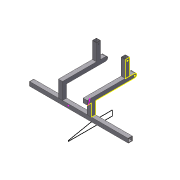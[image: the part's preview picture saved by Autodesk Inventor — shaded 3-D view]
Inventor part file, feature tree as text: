
AUTODESK INVENTOR PART (.ipt)
format: ipt  version: 2012 (Build 160160000, 160)  size: 230,912 bytes
history: native  units: in
note: dims shown in document units (in); Inventor stores cm internally (conversion verified against a paired STEP export)
features: sketch x8, extrude x7, shell x2, pattern_linear x2, plane x1, fillet x1
ambient origin geometry x8: Origin, YZ Plane, XZ Plane, XY Plane, X Axis, Y Axis, Z Axis, Center Point
bodies: Solid1 (feature_tree)
feature tree (21):
  extrude  "Extrusion1"  Depth=1.0in
  shell  "Shell1"  Thickness=24.0in
  plane  "Work Plane1"
  extrude  "Extrusion3"  [1 undecoded]
  pattern_linear  "Rectangular Pattern2"  Count1=2 Spacing1=7.0in
  shell  "Shell3"  Thickness=0.0625in
  extrude  "Extrusion6"  Depth=0.5in
  extrude  "Extrusion9"  Depth=0.5in
  extrude  "Extrusion14"  Depth=0.25in
  pattern_linear  "Rectangular Pattern5"  Spacing1=0.0625in  [1 undecoded]
  extrude  "Extrusion10"  Depth=1.0in
  fillet  "Fillet1"  Radius=1.75in
  extrude  "Extrusion15"  Depth=0.0626in
  sketch  "Sketch15"  dims[d21=1.0in d22=0.0in d23=0.7874in d25=7.0in d26=0.0625in d40=0.5in d41=0.5in d42=0.25in d43=0.0625in d44=0.0in d56=1.0in d57=1.75in d60=0.0626in d61=0.0626in d62=0.0625in d63=0.0625in d64=4.0in d65=0.0in d66=0.7874in d68=7.0in d69=0.25in d70=0.5in d71=0.5in d72=4.0in d73=0.0in d74=0.5in d93=1.0in d94=0.0in d97=0.5in d98=24.0in d99=0.0in d102=4.5in d103=2.0in d104=0.0312in d108=1.0in d109=1.0in d110=0.0in d111=1.0in]
  sketch  "Sketch1"  dims[d0=1.0in d1=1.0in d2=24.0in d3=0.0in]
  sketch  "Sketch3"  dims[d4=0.0625in d14=-9.0in]
  sketch  "Sketch6"  dims[d16=1.0in]
  sketch  "Sketch8"  dims[d17=1.0in]
  sketch  "Sketch9"  dims[d18=90.0deg]
  sketch  "Sketch13"  dims[d19=3.0in]
  sketch  "Sketch14"  dims[d20=11.0in]
note: 2 required parameter values undecoded (feature->parameter linkage not recoverable at this tier; creation-order binding heuristic only, values carry confidence <= 0.55)
